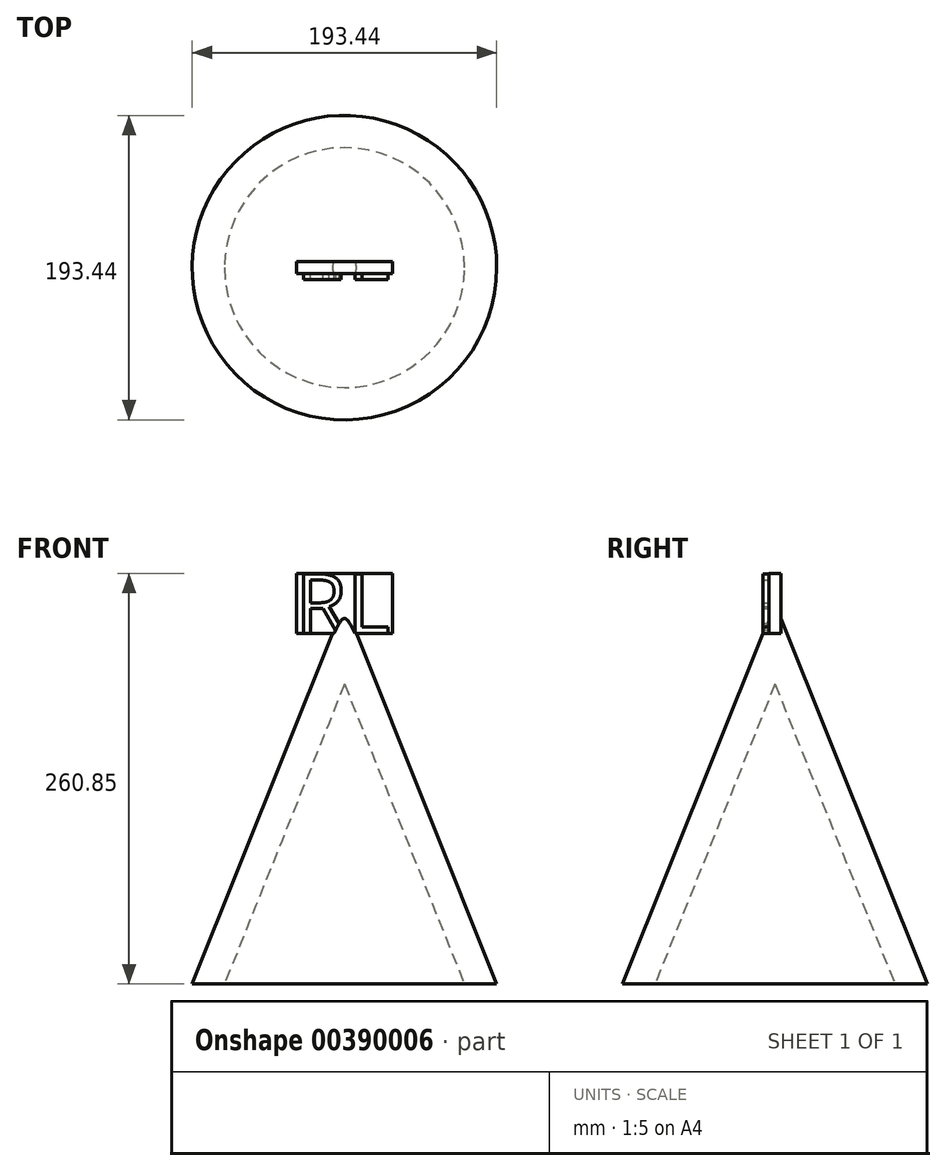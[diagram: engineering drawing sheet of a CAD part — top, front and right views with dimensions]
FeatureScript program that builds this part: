
annotation { "Feature Type Name" : "Feature", "Feature Type Description" : "" }
export const myFeature = defineFeature(function(context is Context, id is Id, definition is map)
    precondition{}
    {
        {
            var Q0;
            Q0=qCreatedBy(makeId("Front.planeOp"),FACE);
            var sketch = newSketch(context, id + "F0", { "sketchPlane" : qUnion([Q0])});
            skLineSegment(sketch, "E0", {"start": v(25.4, 0) * mm, "end": v(32.24, 0) * mm});
            skLineSegment(sketch, "E1", {"start": v(32.24, 0) * mm, "end": v(0, 80.6) * mm});
            skLineSegment(sketch, "E2", {"start": v(0, 80.6) * mm, "end": v(0, 63.5) * mm});
            skLineSegment(sketch, "E3", {"start": v(0, 63.5) * mm, "end": v(25.4, 0) * mm});
            skSolve(sketch);
        }
        {
            var Q0;
            Q0=makeQuery(id+"F0.imprint","IMPRINT",FACE,{"disambiguationData":[TD([[makeQuery(id+"F0.imprint","IMPRINT",EDGE,{"derivedFrom":sQuery(id+"F0.wireOp",EDGE,"E0")}),1.0]])]});
            var Q1;
            Q1=sQuery(id+"F0.wireOp",EDGE,"E2");
            revolve(context, id + "F1", {"entities" : qUnion([Q0]), "axis" : qUnion([Q1]), "revolveType" : RevolveType.FULL});
        }
        {
            var Q0;
            Q0=qCreatedBy(makeId("Front.planeOp"),FACE);
            var sketch = newSketch(context, id + "F2", { "sketchPlane" : qUnion([Q0])});
            skLineSegment(sketch, "E4.bottom", {"start": v(10.16, 86.95) * mm, "end": v(-10.16, 86.95) * mm});
            skLineSegment(sketch, "E4.top", {"start": v(10.16, 74.25) * mm, "end": v(-10.16, 74.25) * mm});
            skLineSegment(sketch, "E4.left", {"start": v(10.16, 86.95) * mm, "end": v(10.16, 74.25) * mm});
            skLineSegment(sketch, "E4.right", {"start": v(-10.16, 86.95) * mm, "end": v(-10.16, 74.25) * mm});
            skPoint(sketch, "E4.middle", {"position": v(0, 80.6) * mm});
            skSolve(sketch);
        }
        {
            var Q0;
            Q0=makeQuery(id+"F2.imprint","IMPRINT",FACE,{"disambiguationData":[TD([[makeQuery(id+"F2.imprint","IMPRINT",EDGE,{"derivedFrom":sQuery(id+"F2.wireOp",EDGE,"E4.bottom")}),1.0]])]});
            extrude(context, id + "F3", {"entities" : qUnion([Q0]), "operationType" : NewBodyOperationType.ADD, "depth" : 2.54 * mm, "symmetric" : true});
        }
        {
            var Q0;
            Q0=makeQuery(id+"F3.opExtrude","CAP_FACE",FACE,{"disambiguationData":[OSD([sQuery(id+"F2.wireOp",EDGE,"E4.bottom"),sQuery(id+"F2.wireOp",EDGE,"E4.top"),sQuery(id+"F2.wireOp",EDGE,"E4.left"),sQuery(id+"F2.wireOp",EDGE,"E4.right")])],"isStart":false});
            var sketch = newSketch(context, id + "F4", { "sketchPlane" : qUnion([Q0])});
            skText(sketch, "E5", { "text": "RL", "fontName": "OpenSans-Regular.ttf"});
            const initialGuessF4  = {"E5": [-0.0104, 0.07425, 1, 0, 0.0127]};
            skSetInitialGuess(sketch, initialGuessF4);
            skSolve(sketch);
        }
        {
            var Q0;
            Q0=makeQuery(id+"F4.imprint","IMPRINT",FACE,{"disambiguationData":[TD([[makeQuery(id+"F4.imprint","IMPRINT",EDGE,{"derivedFrom":sQuery(id+"F4.wireOp",EDGE,"E5.sketch_text.stroke-0")}),-1.0]])]});
            var Q1;
            Q1=makeQuery(id+"F4.imprint","IMPRINT",FACE,{"disambiguationData":[TD([[makeQuery(id+"F4.imprint","IMPRINT",EDGE,{"derivedFrom":sQuery(id+"F4.wireOp",EDGE,"E5.sketch_text.stroke-18")}),-1.0]])]});
            extrude(context, id + "F5", {"entities" : qUnion([Q0, Q1]), "operationType" : NewBodyOperationType.ADD, "depth" : 1.27 * mm});
        }
        {
            var Q0;
            Q0=makeQuery(id+"F1.opRevolve","SWEPT_BODY",BODY,{"disambiguationData":[OSD([sQuery(id+"F0.wireOp",EDGE,"E0"),sQuery(id+"F0.wireOp",EDGE,"E1"),sQuery(id+"F0.wireOp",EDGE,"E2"),sQuery(id+"F0.wireOp",EDGE,"E3")])]});
            var Q1;
            Q1=makeQuery(id+"F3.opExtrude","CAP_VERTEX",VERTEX,{"disambiguationData":[OSD([sQuery(id+"F2.wireOp",EDGE,"E4.bottom"),sQuery(id+"F2.wireOp",EDGE,"E4.right")])],"isStart":false});
            transform(context, id + "F6", {"entities" : qUnion([Q0]), "transformType" : TransformType.SCALE_UNIFORMLY, "scale" : 3, "scalePoint" : qUnion([Q1]), "makeCopy" : false});
        }
    });
